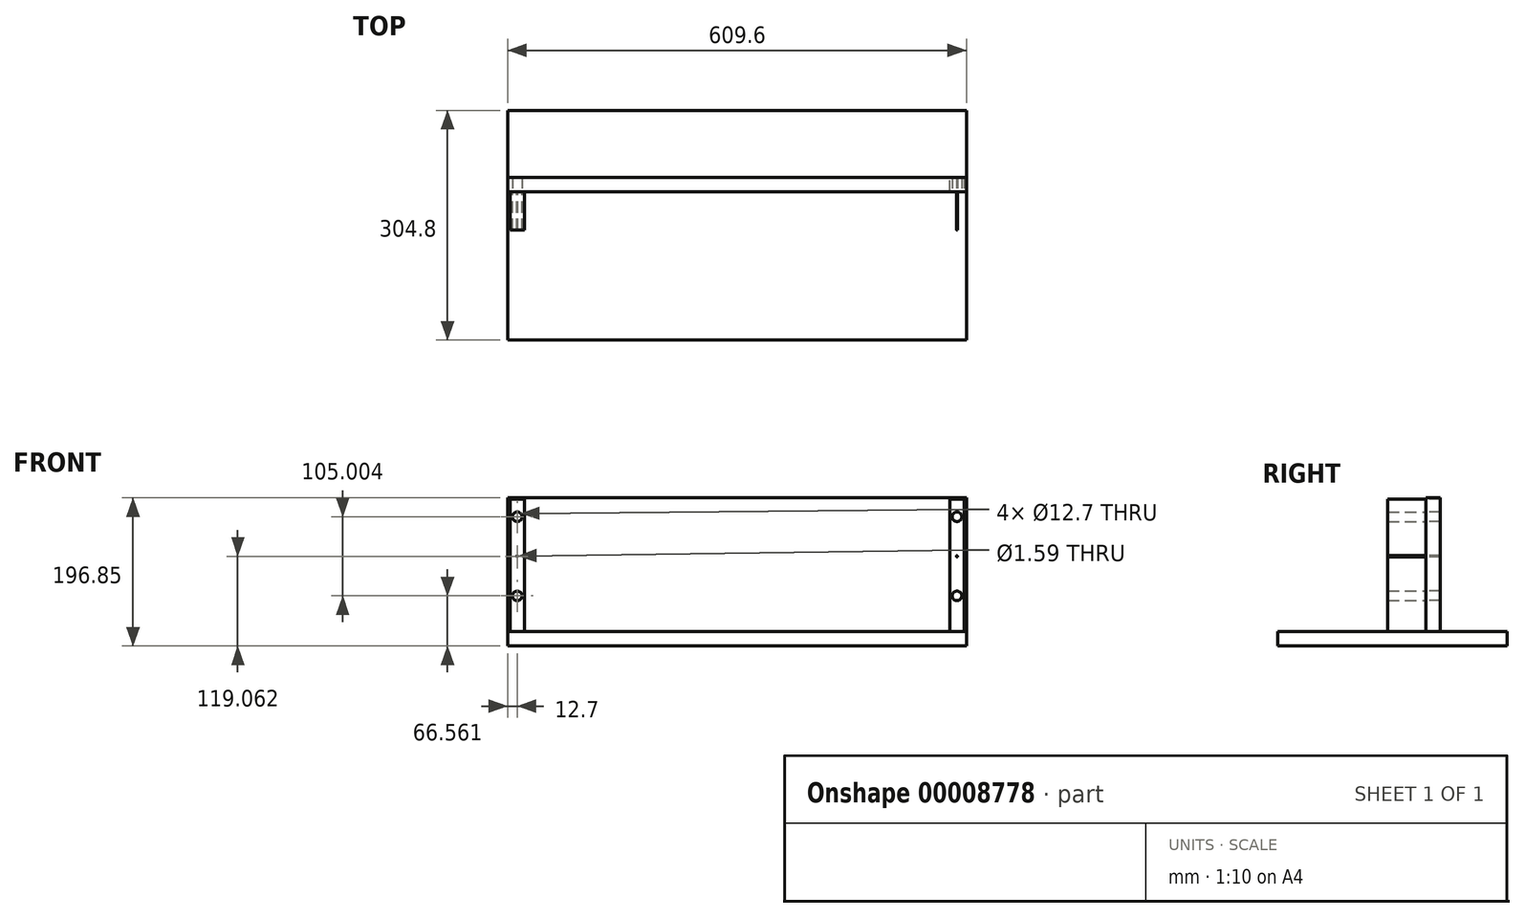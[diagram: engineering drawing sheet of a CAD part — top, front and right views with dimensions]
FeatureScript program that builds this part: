
annotation { "Feature Type Name" : "Feature", "Feature Type Description" : "" }
export const myFeature = defineFeature(function(context is Context, id is Id, definition is map)
    precondition{}
    {
        {
            var Q0;
            Q0=qCreatedBy(makeId("Top.planeOp"),FACE);
            var sketch = newSketch(context, id + "F0", { "sketchPlane" : qUnion([Q0])});
            skLineSegment(sketch, "E0.rect.bottom", {"start": v(304.8, 152.4) * mm, "end": v(-304.8, 152.4) * mm});
            skLineSegment(sketch, "E0.rect.top", {"start": v(304.8, -152.4) * mm, "end": v(-304.8, -152.4) * mm});
            skLineSegment(sketch, "E0.rect.left", {"start": v(304.8, 152.4) * mm, "end": v(304.8, -152.4) * mm});
            skLineSegment(sketch, "E0.rect.right", {"start": v(-304.8, 152.4) * mm, "end": v(-304.8, -152.4) * mm});
            skPoint(sketch, "E0.rect.middle", {"position": v(0, 0) * mm});
            skSolve(sketch);
        }
        {
            var Q0;
            Q0=makeQuery(id+"F0.imprint","IMPRINT",FACE,{"disambiguationData":[TD([[makeQuery(id+"F0.imprint","IMPRINT",EDGE,{"derivedFrom":sQuery(id+"F0.wireOp",EDGE,"E0.rect.bottom")}),1.0]])]});
            extrude(context, id + "F1", {"entities" : qUnion([Q0]), "depth" : 19.05 * mm});
        }
        {
            var Q0;
            Q0=makeQuery(id+"F1.opExtrude","CAP_FACE",FACE,{"disambiguationData":[OSD([sQuery(id+"F0.wireOp",EDGE,"E0.rect.bottom"),sQuery(id+"F0.wireOp",EDGE,"E0.rect.top"),sQuery(id+"F0.wireOp",EDGE,"E0.rect.left"),sQuery(id+"F0.wireOp",EDGE,"E0.rect.right")])],"isStart":false});
            var sketch = newSketch(context, id + "F2", { "sketchPlane" : qUnion([Q0])});
            skLineSegment(sketch, "E1.0", {"start": v(-304.8, 152.4) * mm, "end": v(-304.8, -152.4) * mm, "construction": true});
            skLineSegment(sketch, "E2.0", {"start": v(304.8, -152.4) * mm, "end": v(-304.8, -152.4) * mm, "construction": true});
            skLineSegment(sketch, "E3.bottom", {"start": v(-304.8, -152.4) * mm, "end": v(304.8, -152.4) * mm});
            skLineSegment(sketch, "E3.top", {"start": v(-304.8, -133.35) * mm, "end": v(304.8, -133.35) * mm});
            skLineSegment(sketch, "E3.left", {"start": v(-304.8, -152.4) * mm, "end": v(-304.8, -133.35) * mm});
            skLineSegment(sketch, "E3.right", {"start": v(304.8, -152.4) * mm, "end": v(304.8, -133.35) * mm});
            skLineSegment(sketch, "E4.bottom", {"start": v(-289.46, -133.35) * mm, "end": v(-251.36, -133.35) * mm});
            skLineSegment(sketch, "E4.top", {"start": v(-289.46, 44.45) * mm, "end": v(-251.36, 44.45) * mm});
            skLineSegment(sketch, "E4.left", {"start": v(-289.46, -133.35) * mm, "end": v(-289.46, 44.45) * mm});
            skLineSegment(sketch, "E4.right", {"start": v(-251.36, -133.35) * mm, "end": v(-251.36, 44.45) * mm});
            skLineSegment(sketch, "E5.bottom", {"start": v(-304.8, 44.45) * mm, "end": v(304.8, 44.45) * mm});
            skLineSegment(sketch, "E5.top", {"start": v(-304.8, 63.5) * mm, "end": v(304.8, 63.5) * mm});
            skLineSegment(sketch, "E5.left", {"start": v(-304.8, 44.45) * mm, "end": v(-304.8, 63.5) * mm});
            skLineSegment(sketch, "E5.right", {"start": v(304.8, 44.45) * mm, "end": v(304.8, 63.5) * mm});
            skLineSegment(sketch, "E6", {"start": v(-251.36, -44.45) * mm, "end": v(251.36, -44.45) * mm, "construction": true});
            skLineSegment(sketch, "E7", {"start": v(0, -44.45) * mm, "end": v(0, 0) * mm, "construction": true});
            skLineSegment(sketch, "E8.0.MirrorCS", {"start": v(251.36, -133.35) * mm, "end": v(251.36, 44.45) * mm});
            skLineSegment(sketch, "E9.0.MirrorCS", {"start": v(289.46, -133.35) * mm, "end": v(251.36, -133.35) * mm});
            skLineSegment(sketch, "E10.0.MirrorCS", {"start": v(289.46, -133.35) * mm, "end": v(289.46, 44.45) * mm});
            skLineSegment(sketch, "E11.0.MirrorCS", {"start": v(289.46, 44.45) * mm, "end": v(251.36, 44.45) * mm});
            skLineSegment(sketch, "E12", {"start": v(-270.4, -2.95) * mm, "end": v(-270.4, -107.95) * mm, "construction": true});
            skPoint(sketch, "E13", {"position": v(-270.4, -55.45) * mm});
            skCircle(sketch, "E14", {"center": v(-270.4, -2.95) * mm, "radius": 6.35 * mm});
            skCircle(sketch, "E15.0.MirrorC", {"center": v(-270.4, -107.95) * mm, "radius": 6.35 * mm});
            skCircle(sketch, "E16.0.MirrorC", {"center": v(270.4, -2.95) * mm, "radius": 6.35 * mm});
            skCircle(sketch, "E17.0.MirrorC", {"center": v(270.4, -107.95) * mm, "radius": 6.35 * mm});
            skCircle(sketch, "E18", {"center": v(-270.4, -55.45) * mm, "radius": 0.8 * mm});
            skLineSegment(sketch, "E19", {"start": v(-289.46, -107.95) * mm, "end": v(-251.36, -107.95) * mm, "construction": true});
            skCircle(sketch, "E20.0.MirrorC", {"center": v(270.4, -55.45) * mm, "radius": 0.8 * mm});
            skSolve(sketch);
        }
        {
            var Q0;
            Q0=makeQuery(id+"F2.imprint","IMPRINT",FACE,{"disambiguationData":[TD([[makeQuery(id+"F2.imprint","IMPRINT",EDGE,{"derivedFrom":sQuery(id+"F2.wireOp",EDGE,"E5.top")}),-1.0]])]});
            extrude(context, id + "F3", {"entities" : qUnion([Q0]), "operationType" : NewBodyOperationType.REMOVE, "oppositeDirection" : true, "depth" : 1 / 406.4 * mm});
        }
        {
            var Q0;
            Q0=makeQuery(id+"F3.boolean.opBoolean","COPY",FACE,{"derivedFrom":makeQuery(id+"F3.opExtrude","CAP_FACE",FACE,{"disambiguationData":[OSD([sQuery(id+"F2.wireOp",EDGE,"E5.bottom"),sQuery(id+"F2.wireOp",EDGE,"E5.top"),sQuery(id+"F2.wireOp",EDGE,"E5.left"),sQuery(id+"F2.wireOp",EDGE,"E5.right"),sQuery(id+"F2.wireOp",EDGE,"E11.0.MirrorCS")])],"isStart":false})});
            extrude(context, id + "F4", {"entities" : qUnion([Q0]), "depth" : 177.8 * mm});
        }
        {
            var Q0;
            Q0=makeQuery(id+"F4.opExtrude","SWEPT_FACE",FACE,{"disambiguationData":[OSD([sQuery(id+"F2.wireOp",EDGE,"E5.bottom"),sQuery(id+"F2.wireOp",EDGE,"E11.0.MirrorCS")])]});
            var sketch = newSketch(context, id + "F5", { "sketchPlane" : qUnion([Q0])});
            skLineSegment(sketch, "E21", {"start": v(-292.1, 171.56) * mm, "end": v(-292.1, 66.56) * mm, "construction": true});
            skCircle(sketch, "E22", {"center": v(-292.1, 171.56) * mm, "radius": 6.35 * mm});
            skCircle(sketch, "E23", {"center": v(-292.1, 66.56) * mm, "radius": 6.35 * mm});
            skCircle(sketch, "E24", {"center": v(-292.1, 119.06) * mm, "radius": 0.8 * mm});
            skLineSegment(sketch, "E25", {"start": v(-292.1, 119.06) * mm, "end": v(292.1, 119.06) * mm, "construction": true});
            skLineSegment(sketch, "E26", {"start": v(0, 17.46) * mm, "end": v(0, 119.06) * mm, "construction": true});
            skLineSegment(sketch, "E27.rect.bottom", {"start": v(-282.57, 19.05) * mm, "end": v(-301.63, 19.05) * mm});
            skLineSegment(sketch, "E27.rect.top", {"start": v(-282.58, 195.26) * mm, "end": v(-301.63, 195.26) * mm});
            skLineSegment(sketch, "E27.rect.left", {"start": v(-282.58, 19.05) * mm, "end": v(-282.58, 195.26) * mm});
            skLineSegment(sketch, "E27.rect.right", {"start": v(-301.63, 19.05) * mm, "end": v(-301.63, 195.26) * mm});
            skCircle(sketch, "E28.0.MirrorC", {"center": v(292.1, 119.06) * mm, "radius": 0.8 * mm});
            skCircle(sketch, "E28.1.MirrorC", {"center": v(292.1, 171.56) * mm, "radius": 6.35 * mm});
            skLineSegment(sketch, "E28.2.MirrorCS", {"start": v(282.57, 19.05) * mm, "end": v(301.63, 19.05) * mm});
            skCircle(sketch, "E28.3.MirrorC", {"center": v(292.1, 66.56) * mm, "radius": 6.35 * mm});
            skLineSegment(sketch, "E28.4.MirrorCS", {"start": v(282.58, 19.05) * mm, "end": v(282.58, 195.26) * mm});
            skLineSegment(sketch, "E28.5.MirrorCS", {"start": v(282.58, 195.26) * mm, "end": v(301.63, 195.26) * mm});
            skLineSegment(sketch, "E28.6.MirrorCS", {"start": v(301.63, 19.05) * mm, "end": v(301.63, 195.26) * mm});
            skLineSegment(sketch, "E29.0", {"start": v(-304.8, 19.05) * mm, "end": v(304.8, 19.05) * mm});
            skLineSegment(sketch, "E30", {"start": v(-292.1, 195.26) * mm, "end": v(-292.1, 19.05) * mm, "construction": true});
            skSolve(sketch);
        }
        {
            var Q0;
            Q0=makeQuery(id+"F5.imprint","IMPRINT",FACE,{"disambiguationData":[TD([[makeQuery(id+"F5.imprint","IMPRINT",EDGE,{"derivedFrom":sQuery(id+"F5.wireOp",EDGE,"E22")}),1.0]])]});
            var Q1;
            Q1=makeQuery(id+"F5.imprint","IMPRINT",FACE,{"disambiguationData":[TD([[makeQuery(id+"F5.imprint","IMPRINT",EDGE,{"derivedFrom":sQuery(id+"F5.wireOp",EDGE,"E23")}),1.0]])]});
            var Q2;
            Q2=makeQuery(id+"F5.imprint","IMPRINT",FACE,{"disambiguationData":[TD([[makeQuery(id+"F5.imprint","IMPRINT",EDGE,{"derivedFrom":sQuery(id+"F5.wireOp",EDGE,"E28.3.MirrorC")}),-1.0]])]});
            var Q3;
            Q3=makeQuery(id+"F5.imprint","IMPRINT",FACE,{"disambiguationData":[TD([[makeQuery(id+"F5.imprint","IMPRINT",EDGE,{"derivedFrom":sQuery(id+"F5.wireOp",EDGE,"E28.1.MirrorC")}),-1.0]])]});
            extrude(context, id + "F6", {"entities" : qUnion([Q0, Q1, Q2, Q3]), "operationType" : NewBodyOperationType.REMOVE, "endBound" : BoundingType.UP_TO_NEXT, "oppositeDirection" : true, "depth" : 25.4 * mm});
        }
        {
            var Q0;
            Q0=makeQuery(id+"F5.imprint","IMPRINT",FACE,{"disambiguationData":[TD([[makeQuery(id+"F5.imprint","IMPRINT",EDGE,{"derivedFrom":sQuery(id+"F5.wireOp",EDGE,"E22")}),-1.0]])]});
            var Q1;
            Q1=makeQuery(id+"F5.imprint","IMPRINT",FACE,{"disambiguationData":[TD([[makeQuery(id+"F5.imprint","IMPRINT",EDGE,{"derivedFrom":sQuery(id+"F5.wireOp",EDGE,"E28.0.MirrorC")}),1.0]])]});
            extrude(context, id + "F7", {"entities" : qUnion([Q0, Q1]), "depth" : 50.8 * mm});
        }
    });
